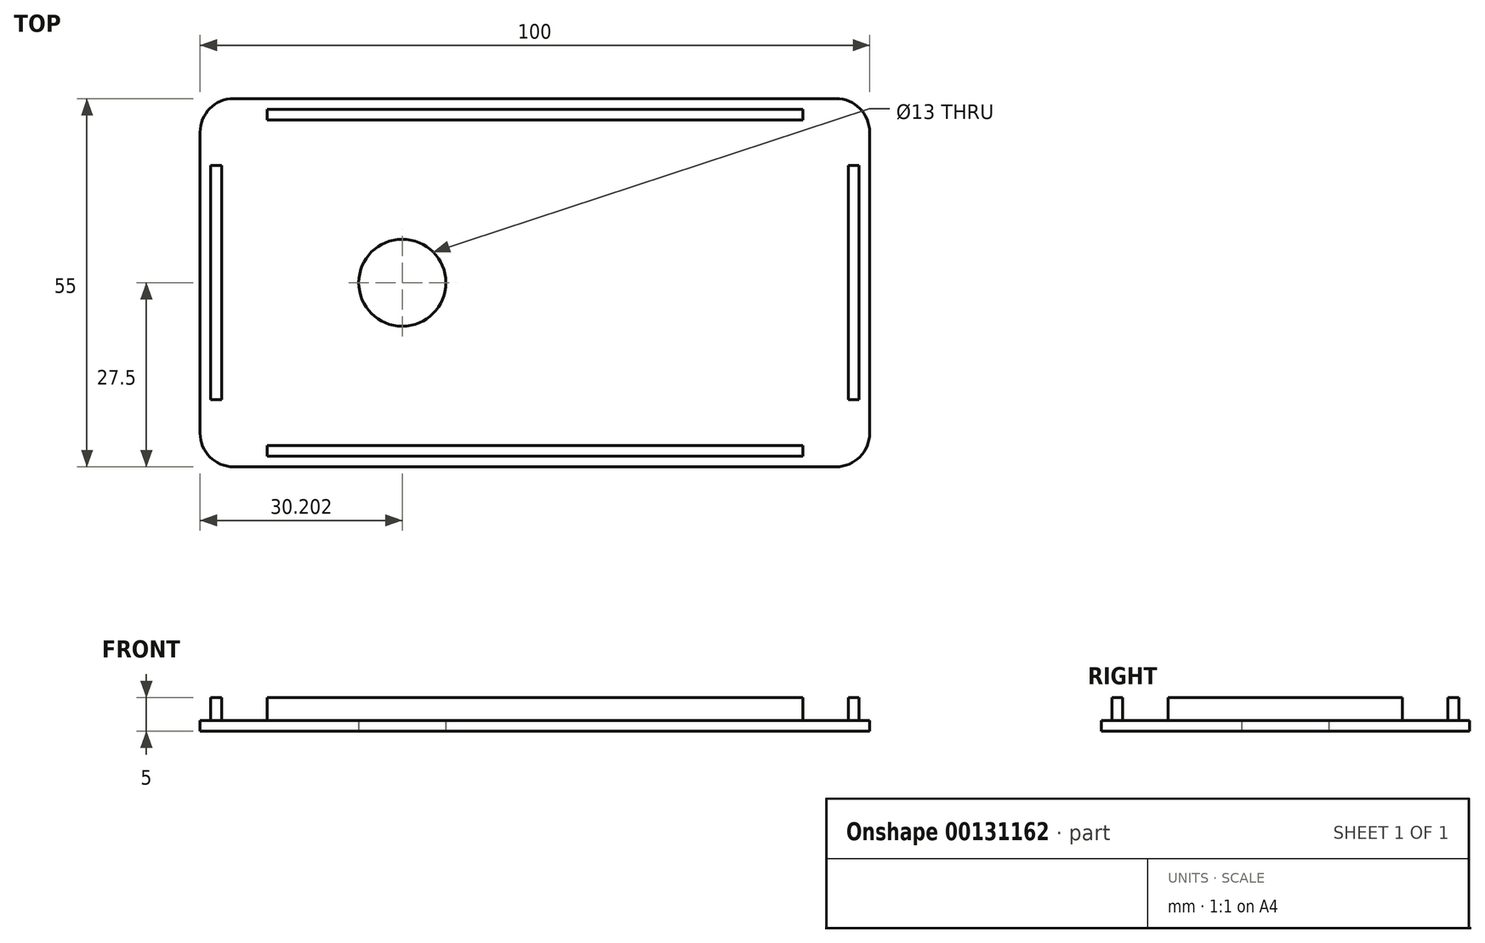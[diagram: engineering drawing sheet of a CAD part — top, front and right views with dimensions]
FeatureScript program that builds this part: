
annotation { "Feature Type Name" : "Feature", "Feature Type Description" : "" }
export const myFeature = defineFeature(function(context is Context, id is Id, definition is map)
    precondition{}
    {
        {
            var Q0;
            Q0=qCreatedBy(makeId("Top.planeOp"),FACE);
            var sketch = newSketch(context, id + "F0", { "sketchPlane" : qUnion([Q0])});
            skLineSegment(sketch, "E0.bottom", {"start": v(50, -27.5) * mm, "end": v(-50, -27.5) * mm});
            skLineSegment(sketch, "E0.top", {"start": v(50, 27.5) * mm, "end": v(-50, 27.5) * mm});
            skLineSegment(sketch, "E0.left", {"start": v(50, -27.5) * mm, "end": v(50, 27.5) * mm});
            skLineSegment(sketch, "E0.right", {"start": v(-50, -27.5) * mm, "end": v(-50, 27.5) * mm});
            skPoint(sketch, "E0.middle", {"position": v(0, 0) * mm});
            skLineSegment(sketch, "E1.bottom", {"start": v(48.4, -25.9) * mm, "end": v(-48.4, -25.9) * mm, "construction": true});
            skLineSegment(sketch, "E1.top", {"start": v(48.4, 25.9) * mm, "end": v(-48.4, 25.9) * mm, "construction": true});
            skLineSegment(sketch, "E1.left", {"start": v(48.4, -25.9) * mm, "end": v(48.4, 25.9) * mm, "construction": true});
            skLineSegment(sketch, "E1.right", {"start": v(-48.4, -25.9) * mm, "end": v(-48.4, 25.9) * mm, "construction": true});
            skLineSegment(sketch, "E2.bottom", {"start": v(46.8, -24.3) * mm, "end": v(-46.8, -24.3) * mm, "construction": true});
            skLineSegment(sketch, "E2.top", {"start": v(46.8, 24.3) * mm, "end": v(-46.8, 24.3) * mm, "construction": true});
            skLineSegment(sketch, "E2.left", {"start": v(46.8, -24.3) * mm, "end": v(46.8, 24.3) * mm, "construction": true});
            skLineSegment(sketch, "E2.right", {"start": v(-46.8, -24.3) * mm, "end": v(-46.8, 24.3) * mm, "construction": true});
            skLineSegment(sketch, "E3.bottom", {"start": v(40, 24.3) * mm, "end": v(-40, 24.3) * mm});
            skLineSegment(sketch, "E3.top", {"start": v(40, 25.9) * mm, "end": v(-40, 25.9) * mm});
            skLineSegment(sketch, "E3.left", {"start": v(40, 24.3) * mm, "end": v(40, 25.9) * mm});
            skLineSegment(sketch, "E3.right", {"start": v(-40, 24.3) * mm, "end": v(-40, 25.9) * mm});
            skLineSegment(sketch, "E4.MirrorCS", {"start": v(-40, -24.3) * mm, "end": v(-40, -25.9) * mm});
            skLineSegment(sketch, "E5.MirrorCS", {"start": v(40, -24.3) * mm, "end": v(40, -25.9) * mm});
            skLineSegment(sketch, "E6", {"start": v(-40, -24.3) * mm, "end": v(40, -24.3) * mm});
            skLineSegment(sketch, "E7", {"start": v(40, -25.9) * mm, "end": v(-40, -25.9) * mm});
            skLineSegment(sketch, "E8.bottom", {"start": v(46.8, 17.5) * mm, "end": v(48.4, 17.5) * mm});
            skLineSegment(sketch, "E8.top", {"start": v(46.8, -17.5) * mm, "end": v(48.4, -17.5) * mm});
            skLineSegment(sketch, "E8.left", {"start": v(46.8, 17.5) * mm, "end": v(46.8, -17.5) * mm});
            skLineSegment(sketch, "E8.right", {"start": v(48.4, 17.5) * mm, "end": v(48.4, -17.5) * mm});
            skLineSegment(sketch, "E9.MirrorCS", {"start": v(-46.8, 17.5) * mm, "end": v(-48.4, 17.5) * mm});
            skLineSegment(sketch, "E10.MirrorCS", {"start": v(-46.8, -17.5) * mm, "end": v(-48.4, -17.5) * mm});
            skLineSegment(sketch, "E11", {"start": v(-48.4, 17.5) * mm, "end": v(-48.4, -17.5) * mm});
            skLineSegment(sketch, "E12", {"start": v(-46.8, 17.5) * mm, "end": v(-46.8, -17.5) * mm});
            skSolve(sketch);
        }
        {
            var Q0;
            Q0=makeQuery(id+"F0.imprint","IMPRINT",FACE,{"disambiguationData":[TD([[makeQuery(id+"F0.imprint","IMPRINT",EDGE,{"derivedFrom":sQuery(id+"F0.wireOp",EDGE,"E8.bottom")}),-1.0]])]});
            var Q1;
            Q1=makeQuery(id+"F0.imprint","IMPRINT",FACE,{"disambiguationData":[TD([[makeQuery(id+"F0.imprint","IMPRINT",EDGE,{"derivedFrom":sQuery(id+"F0.wireOp",EDGE,"E4.MirrorCS")}),1.0]])]});
            var Q2;
            Q2=makeQuery(id+"F0.imprint","IMPRINT",FACE,{"disambiguationData":[TD([[makeQuery(id+"F0.imprint","IMPRINT",EDGE,{"derivedFrom":sQuery(id+"F0.wireOp",EDGE,"E3.bottom")}),-1.0]])]});
            var Q3;
            Q3=makeQuery(id+"F0.imprint","IMPRINT",FACE,{"disambiguationData":[TD([[makeQuery(id+"F0.imprint","IMPRINT",EDGE,{"derivedFrom":sQuery(id+"F0.wireOp",EDGE,"E9.MirrorCS")}),1.0]])]});
            extrude(context, id + "F1", {"entities" : qUnion([Q0, Q1, Q2, Q3]), "depth" : 3.4 * mm});
        }
        {
            var Q0;
            Q0=qCreatedBy(makeId("Top.planeOp"),FACE);
            var sketch = newSketch(context, id + "F2", { "sketchPlane" : qUnion([Q0])});
            skLineSegment(sketch, "E13.bottom", {"start": v(50, -27.5) * mm, "end": v(-50, -27.5) * mm});
            skLineSegment(sketch, "E13.top", {"start": v(50, 27.5) * mm, "end": v(-50, 27.5) * mm});
            skLineSegment(sketch, "E13.left", {"start": v(50, -27.5) * mm, "end": v(50, 27.5) * mm});
            skLineSegment(sketch, "E13.right", {"start": v(-50, -27.5) * mm, "end": v(-50, 27.5) * mm});
            skPoint(sketch, "E13.middle", {"position": v(0, 0) * mm});
            skSolve(sketch);
        }
        {
            var Q0;
            Q0 = qSketchRegion(id + "F2", true);
            extrude(context, id + "F3", {"entities" : qUnion([Q0]), "oppositeDirection" : true, "depth" : 1.6 * mm});
        }
        {
            var Q0;
            Q0=makeQuery(id+"F3.opExtrude","SWEPT_EDGE",EDGE,{"disambiguationData":[OSD([sQuery(id+"F2.wireOp",EDGE,"E13.bottom"),sQuery(id+"F2.wireOp",EDGE,"E13.right")])]});
            var Q1;
            Q1=makeQuery(id+"F3.opExtrude","SWEPT_EDGE",EDGE,{"disambiguationData":[OSD([sQuery(id+"F2.wireOp",EDGE,"E13.bottom"),sQuery(id+"F2.wireOp",EDGE,"E13.left")])]});
            var Q2;
            Q2=makeQuery(id+"F3.opExtrude","SWEPT_EDGE",EDGE,{"disambiguationData":[OSD([sQuery(id+"F2.wireOp",EDGE,"E13.top"),sQuery(id+"F2.wireOp",EDGE,"E13.left")])]});
            var Q3;
            Q3=makeQuery(id+"F3.opExtrude","SWEPT_EDGE",EDGE,{"disambiguationData":[OSD([sQuery(id+"F2.wireOp",EDGE,"E13.top"),sQuery(id+"F2.wireOp",EDGE,"E13.right")])]});
            fillet(context, id + "F4", {"entities" : qUnion([Q0, Q1, Q2, Q3]), "radius" : 5 * mm, "tangentPropagation" : true, "allowEdgeOverflow" : false});
        }
        {
            var Q0;
            Q0=makeQuery(id+"F3.opExtrude","CAP_FACE",FACE,{"disambiguationData":[OSD([sQuery(id+"F2.wireOp",EDGE,"E13.bottom"),sQuery(id+"F2.wireOp",EDGE,"E13.top"),sQuery(id+"F2.wireOp",EDGE,"E13.left"),sQuery(id+"F2.wireOp",EDGE,"E13.right")])],"isStart":true});
            var sketch = newSketch(context, id + "F5", { "sketchPlane" : qUnion([Q0])});
            skLineSegment(sketch, "E14", {"start": v(50, 0) * mm, "end": v(-50, 0) * mm, "construction": true});
            skCircle(sketch, "E15", {"center": v(-19.8, 0) * mm, "radius": 6.5 * mm});
            skSolve(sketch);
        }
        {
            var Q0;
            Q0=makeQuery(id+"F5.imprint","IMPRINT",FACE,{"disambiguationData":[TD([[makeQuery(id+"F5.imprint","IMPRINT",EDGE,{"derivedFrom":sQuery(id+"F5.wireOp",EDGE,"E15")}),1.0]])]});
            extrude(context, id + "F6", {"entities" : qUnion([Q0]), "operationType" : NewBodyOperationType.REMOVE, "endBound" : BoundingType.SYMMETRIC, "depth" : 5 * mm});
        }
    });
